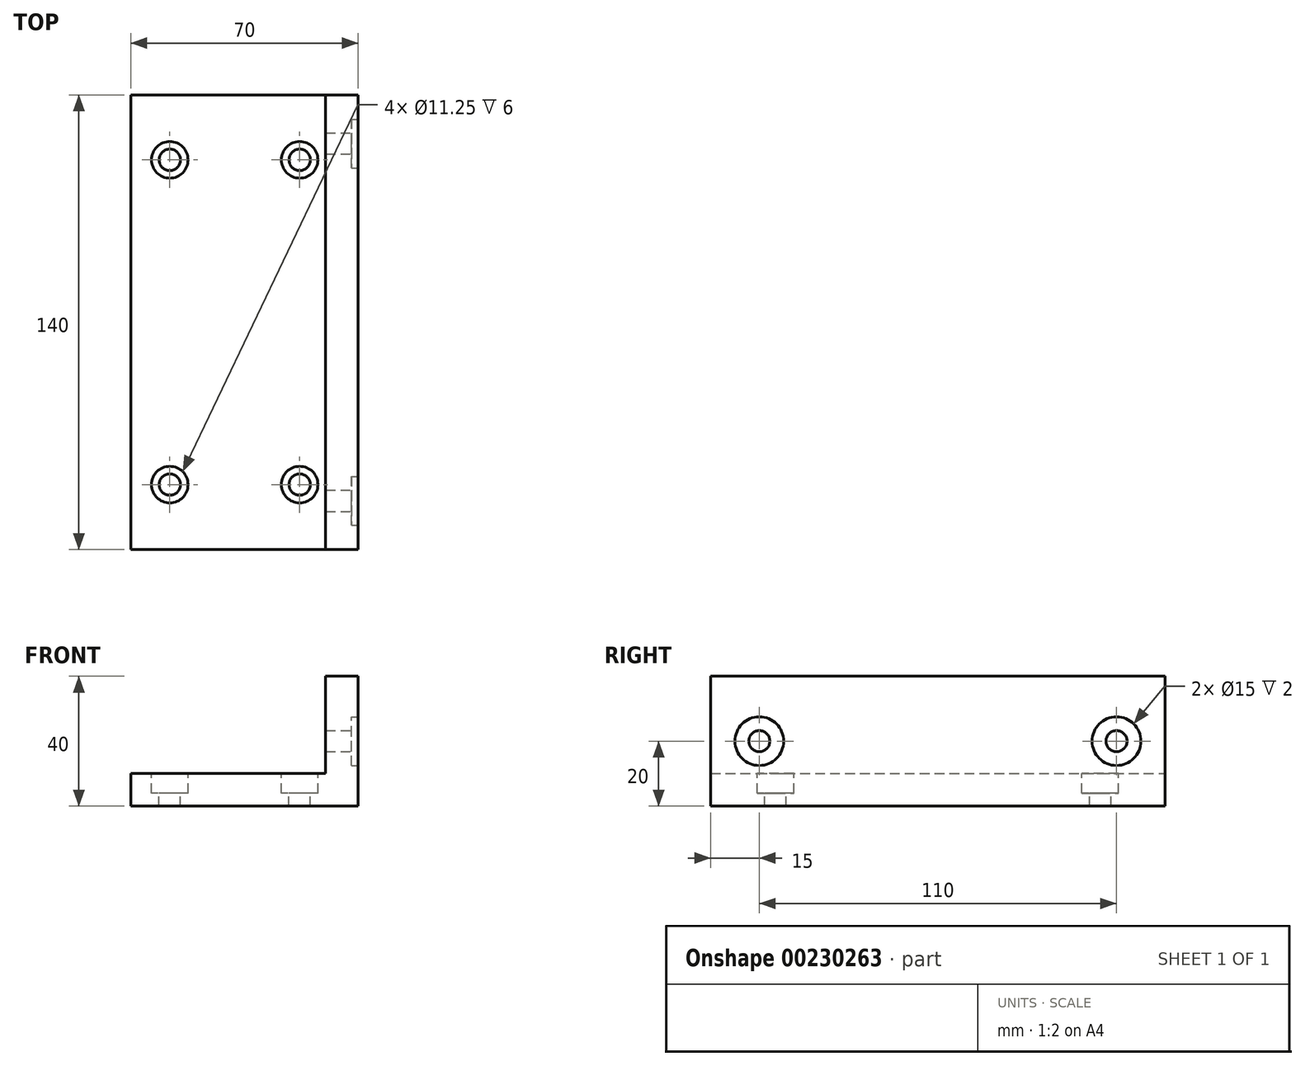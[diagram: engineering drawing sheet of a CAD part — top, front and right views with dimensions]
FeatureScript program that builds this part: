
annotation { "Feature Type Name" : "Feature", "Feature Type Description" : "" }
export const myFeature = defineFeature(function(context is Context, id is Id, definition is map)
    precondition{}
    {
        {
            var Q0;
            Q0=qCreatedBy(makeId("Front.planeOp"),FACE);
            var sketch = newSketch(context, id + "F0", { "sketchPlane" : qUnion([Q0])});
            skLineSegment(sketch, "E0", {"start": v(0, 0) * mm, "end": v(70, 0) * mm});
            skLineSegment(sketch, "E1", {"start": v(70, 0) * mm, "end": v(70, 40) * mm});
            skLineSegment(sketch, "E2", {"start": v(70, 40) * mm, "end": v(60, 40) * mm});
            skLineSegment(sketch, "E3", {"start": v(60, 40) * mm, "end": v(60, 10) * mm});
            skLineSegment(sketch, "E4", {"start": v(60, 10) * mm, "end": v(0, 10) * mm});
            skLineSegment(sketch, "E5", {"start": v(0, 10) * mm, "end": v(0, 0) * mm});
            skSolve(sketch);
        }
        {
            var Q0;
            Q0=makeQuery(id+"F0.imprint","IMPRINT",FACE,{"disambiguationData":[TD([[makeQuery(id+"F0.imprint","IMPRINT",EDGE,{"derivedFrom":sQuery(id+"F0.wireOp",EDGE,"E0")}),1.0]])]});
            extrude(context, id + "F1", {"entities" : qUnion([Q0]), "endBound" : BoundingType.SYMMETRIC, "depth" : 140 * mm});
        }
        {
            var Q0;
            Q0=makeQuery(id+"F1.opExtrude","SWEPT_FACE",FACE,{"disambiguationData":[OSD([sQuery(id+"F0.wireOp",EDGE,"E4")])]});
            var sketch = newSketch(context, id + "F2", { "sketchPlane" : qUnion([Q0])});
            skPoint(sketch, "E6", {"position": v(12, 50) * mm});
            skPoint(sketch, "E7", {"position": v(52, 50) * mm});
            skPoint(sketch, "E8", {"position": v(12, -50) * mm});
            skPoint(sketch, "E9", {"position": v(52, -50) * mm});
            skSolve(sketch);
        }
        {
            var Q0;
            Q0=sQuery(id+"F2.wireOp",VERTEX,"E6");
            var Q1;
            Q1=sQuery(id+"F2.wireOp",VERTEX,"E7");
            var Q2;
            Q2=sQuery(id+"F2.wireOp",VERTEX,"E9");
            var Q3;
            Q3=sQuery(id+"F2.wireOp",VERTEX,"E8");
            var Q4;
            Q4=makeQuery(id+"F1.opExtrude","SWEPT_BODY",BODY,{"disambiguationData":[OSD([sQuery(id+"F0.wireOp",EDGE,"E0"),sQuery(id+"F0.wireOp",EDGE,"E1"),sQuery(id+"F0.wireOp",EDGE,"E2"),sQuery(id+"F0.wireOp",EDGE,"E3"),sQuery(id+"F0.wireOp",EDGE,"E4"),sQuery(id+"F0.wireOp",EDGE,"E5")])]});
            hole(context, id + "F3", {"style" : HoleStyle.C_BORE, "endStyle" : HoleEndStyle.BLIND, "standardTappedOrClearance" : lookupTablePath({ "standard" : "ISO", "fit" : "Normal", "size" : "M6", "type" : "Clearance" }), "standardBlindInLast" : lookupTablePath({ "fit" : "Standard", "standard" : "ISO", "size" : "M6", "type" : "Clearance" }), "holeDiameter" : 6.6 * mm, "cBoreDiameter" : 11.25 * mm, "cBoreDepth" : 6 * mm, "holeDepth" : 12 * mm, "locations" : qUnion([Q0, Q1, Q2, Q3]), "scope" : qUnion([Q4])});
        }
        {
            var Q0;
            Q0=makeQuery(id+"F1.opExtrude","SWEPT_FACE",FACE,{"disambiguationData":[OSD([sQuery(id+"F0.wireOp",EDGE,"E1")])]});
            var sketch = newSketch(context, id + "F4", { "sketchPlane" : qUnion([Q0])});
            skCircle(sketch, "E10", {"center": v(-55, 20) * mm, "radius": 7.5 * mm});
            skCircle(sketch, "E11", {"center": v(55, 20) * mm, "radius": 7.5 * mm});
            skSolve(sketch);
        }
        {
            var Q0;
            Q0=makeQuery(id+"F4.imprint","IMPRINT",FACE,{"disambiguationData":[TD([[makeQuery(id+"F4.imprint","IMPRINT",EDGE,{"derivedFrom":sQuery(id+"F4.wireOp",EDGE,"E10")}),1.0]])]});
            var Q1;
            Q1=makeQuery(id+"F4.imprint","IMPRINT",FACE,{"disambiguationData":[TD([[makeQuery(id+"F4.imprint","IMPRINT",EDGE,{"derivedFrom":sQuery(id+"F4.wireOp",EDGE,"E11")}),1.0]])]});
            extrude(context, id + "F5", {"entities" : qUnion([Q0, Q1]), "operationType" : NewBodyOperationType.REMOVE, "oppositeDirection" : true, "depth" : 2 * mm});
        }
        {
            var Q0;
            Q0=makeQuery(id+"F5.boolean.opBoolean","COPY",FACE,{"derivedFrom":makeQuery(id+"F5.opExtrude","CAP_FACE",FACE,{"disambiguationData":[OSD([sQuery(id+"F4.wireOp",EDGE,"E10")])],"isStart":false})});
            var sketch = newSketch(context, id + "F6", { "sketchPlane" : qUnion([Q0])});
            skCircle(sketch, "E12", {"center": v(-55, 20) * mm, "radius": 3.25 * mm});
            skSolve(sketch);
        }
        {
            var Q0;
            Q0=makeQuery(id+"F5.boolean.opBoolean","COPY",FACE,{"derivedFrom":makeQuery(id+"F5.opExtrude","CAP_FACE",FACE,{"disambiguationData":[OSD([sQuery(id+"F4.wireOp",EDGE,"E11")])],"isStart":false})});
            var sketch = newSketch(context, id + "F7", { "sketchPlane" : qUnion([Q0])});
            skCircle(sketch, "E13", {"center": v(55, 20) * mm, "radius": 3.25 * mm});
            skSolve(sketch);
        }
        {
            var Q0;
            Q0=makeQuery(id+"F6.imprint","IMPRINT",FACE,{"disambiguationData":[TD([[makeQuery(id+"F6.imprint","IMPRINT",EDGE,{"derivedFrom":sQuery(id+"F6.wireOp",EDGE,"E12")}),1.0]])]});
            var Q1;
            Q1=makeQuery(id+"F7.imprint","IMPRINT",FACE,{"disambiguationData":[TD([[makeQuery(id+"F7.imprint","IMPRINT",EDGE,{"derivedFrom":sQuery(id+"F7.wireOp",EDGE,"E13")}),1.0]])]});
            extrude(context, id + "F8", {"entities" : qUnion([Q0, Q1]), "operationType" : NewBodyOperationType.REMOVE, "oppositeDirection" : true, "depth" : 25 * mm});
        }
    });
